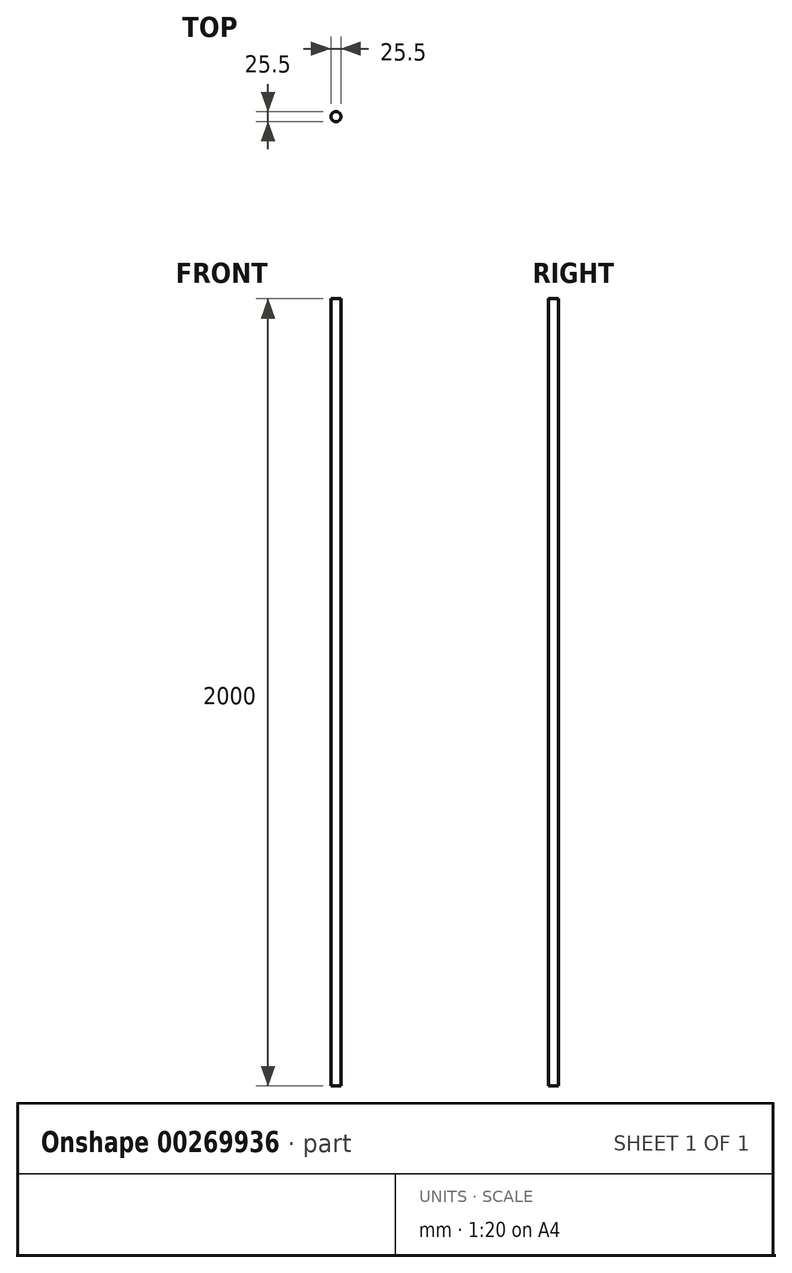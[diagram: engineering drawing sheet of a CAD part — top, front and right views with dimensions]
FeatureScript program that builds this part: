
annotation { "Feature Type Name" : "Feature", "Feature Type Description" : "" }
export const myFeature = defineFeature(function(context is Context, id is Id, definition is map)
    precondition{}
    {
        {
            var Q0;
            Q0=qCreatedBy(makeId("Top.planeOp"),FACE);
            var sketch = newSketch(context, id + "F0", { "sketchPlane" : qUnion([Q0])});
            skCircle(sketch, "E0", {"center": v(0, 0) * mm, "radius": 12.75 * mm});
            skSolve(sketch);
        }
        {
            var Q0;
            Q0 = qSketchRegion(id + "F0", true);
            extrude(context, id + "F1", {"entities" : qUnion([Q0]), "depth" : 2000 * mm});
        }
    });
